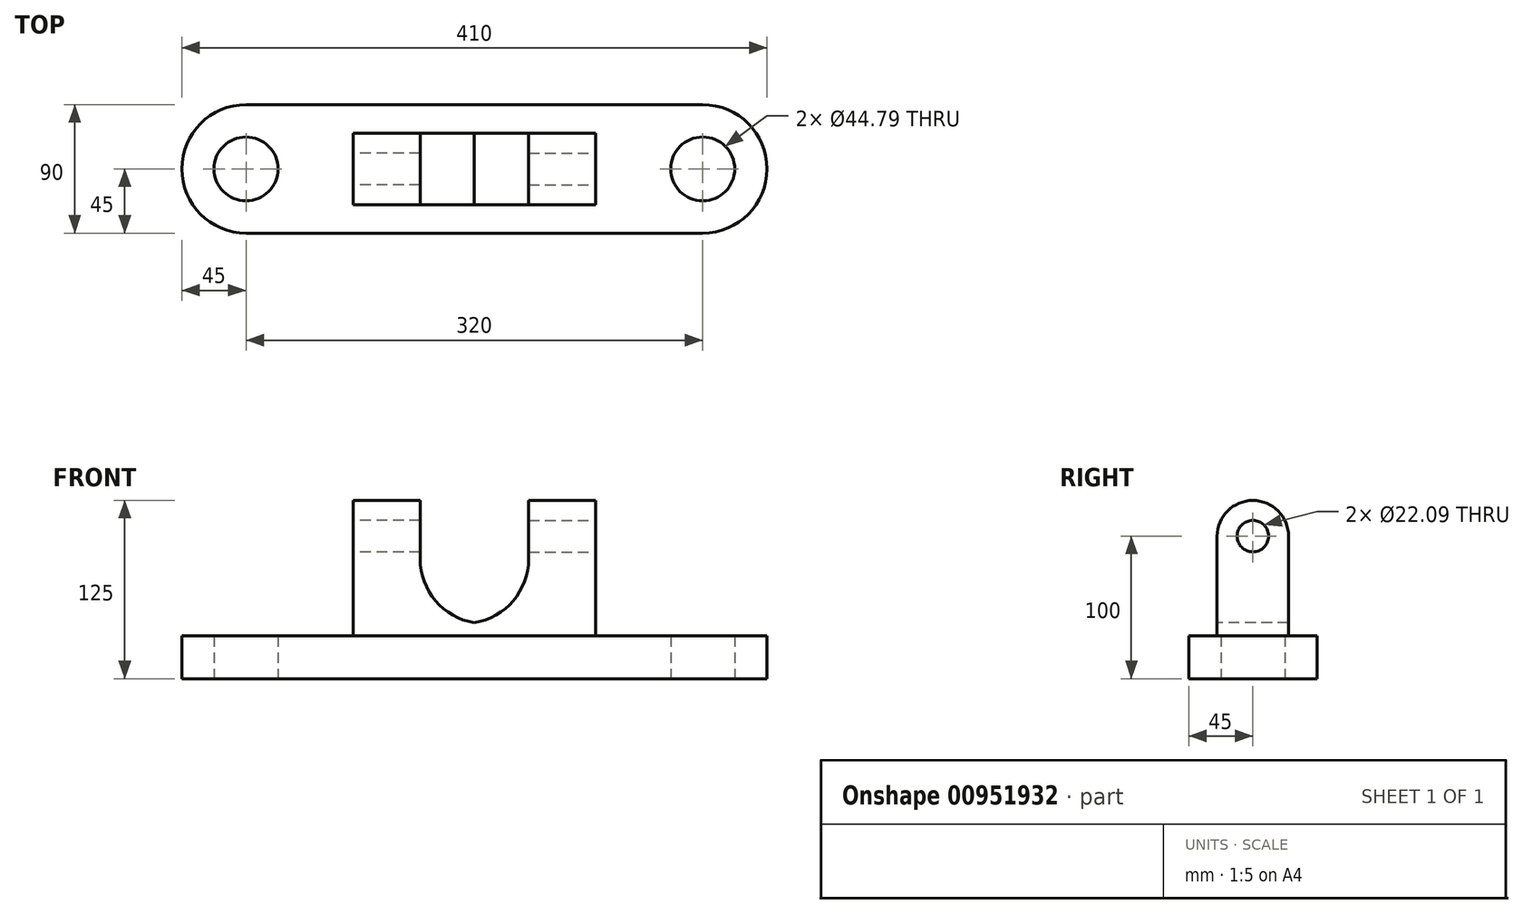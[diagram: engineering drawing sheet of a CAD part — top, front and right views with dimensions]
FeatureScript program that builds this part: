
annotation { "Feature Type Name" : "Feature", "Feature Type Description" : "" }
export const myFeature = defineFeature(function(context is Context, id is Id, definition is map)
    precondition{}
    {
        {
            var Q0;
            Q0=qCreatedBy(makeId("Top.planeOp"),FACE);
            var sketch = newSketch(context, id + "F0", { "sketchPlane" : qUnion([Q0])});
            skLineSegment(sketch, "E0.bottom", {"start": v(0, 45) * mm, "end": v(-160, 45) * mm});
            skLineSegment(sketch, "E0.top", {"start": v(0, -45) * mm, "end": v(-160, -45) * mm});
            skLineSegment(sketch, "E0.left", {"start": v(0, 45) * mm, "end": v(0, -45) * mm});
            skLineSegment(sketch, "E1", {"start": v(0, 45) * mm, "end": v(0, 0) * mm});
            skLineSegment(sketch, "E2", {"start": v(0, -45) * mm, "end": v(0, 0) * mm});
            skArc(sketch, "E3", {"start": v(-160, 45) * mm, "mid": v(-205, 0) * mm, "end": v(-160, -45) * mm});
            skCircle(sketch, "E4", {"center": v(-160, 0) * mm, "radius": 22.4 * mm});
            skSolve(sketch);
        }
        {
            var Q0;
            Q0=makeQuery(id+"F0.imprint","IMPRINT",FACE,{"disambiguationData":[TD([[makeQuery(id+"F0.imprint","IMPRINT",EDGE,{"derivedFrom":sQuery(id+"F0.wireOp",EDGE,"E0.top")}),-1.0]])]});
            extrude(context, id + "F1", {"entities" : qUnion([Q0]), "depth" : 30 * mm, "offsetDistance" : 25 * mm});
        }
        {
            var Q0;
            Q0=makeQuery(id+"F1.opExtrude","CAP_FACE",FACE,{"disambiguationData":[OSD([sQuery(id+"F0.wireOp",EDGE,"E0.top"),sQuery(id+"F0.wireOp",EDGE,"E1"),sQuery(id+"F0.wireOp",EDGE,"E2"),sQuery(id+"F0.wireOp",EDGE,"E0.bottom"),sQuery(id+"F0.wireOp",EDGE,"E3"),sQuery(id+"F0.wireOp",EDGE,"E4")])],"isStart":false});
            var sketch = newSketch(context, id + "F2", { "sketchPlane" : qUnion([Q0])});
            skLineSegment(sketch, "E5", {"start": v(0, 45) * mm, "end": v(0, 25) * mm});
            skLineSegment(sketch, "E6", {"start": v(0, 25) * mm, "end": v(0, -25) * mm});
            skLineSegment(sketch, "E7", {"start": v(0, -25) * mm, "end": v(0, -45) * mm});
            skLineSegment(sketch, "E8", {"start": v(0, -45) * mm, "end": v(0, -25) * mm});
            skLineSegment(sketch, "E9.bottom", {"start": v(0, 25) * mm, "end": v(0, 25) * mm});
            skLineSegment(sketch, "E9.top", {"start": v(0, -25) * mm, "end": v(0, -25) * mm});
            skLineSegment(sketch, "E10.bottom", {"start": v(0, 25) * mm, "end": v(-85, 25) * mm});
            skLineSegment(sketch, "E10.top", {"start": v(0, -25) * mm, "end": v(-85, -25) * mm});
            skLineSegment(sketch, "E10.right", {"start": v(-85, 25) * mm, "end": v(-85, -25) * mm});
            skSolve(sketch);
        }
        {
            var Q0;
            Q0=makeQuery(id+"F2.imprint","IMPRINT",FACE,{"disambiguationData":[TD([[makeQuery(id+"F2.imprint","IMPRINT",EDGE,{"derivedFrom":sQuery(id+"F2.wireOp",EDGE,"E10.bottom")}),1.0]])]});
            extrude(context, id + "F3", {"entities" : qUnion([Q0]), "operationType" : NewBodyOperationType.ADD, "depth" : 70 * mm, "offsetDistance" : 25 * mm});
        }
        {
            var Q0;
            Q0=makeQuery(id+"F3.opExtrude","SWEPT_FACE",FACE,{"disambiguationData":[OSD([sQuery(id+"F2.wireOp",EDGE,"E10.top")])]});
            var sketch = newSketch(context, id + "F4", { "sketchPlane" : qUnion([Q0])});
            skLineSegment(sketch, "E11.bottom", {"start": v(0, 100) * mm, "end": v(-38, 100) * mm});
            skLineSegment(sketch, "E11.top", {"start": v(0, 39.26) * mm, "end": v(-38, 39.26) * mm});
            skLineSegment(sketch, "E11.left", {"start": v(0, 100) * mm, "end": v(0, 39.26) * mm});
            skLineSegment(sketch, "E11.right", {"start": v(-38, 100) * mm, "end": v(-38, 39.26) * mm});
            skLineSegment(sketch, "E12", {"start": v(-85, 100) * mm, "end": v(-38, 100) * mm});
            skSolve(sketch);
        }
        {
            var Q0;
            Q0=makeQuery(id+"F4.imprint","IMPRINT",FACE,{"disambiguationData":[TD([[makeQuery(id+"F4.imprint","IMPRINT",EDGE,{"derivedFrom":sQuery(id+"F4.wireOp",EDGE,"E11.bottom")}),1.0]])]});
            extrude(context, id + "F5", {"entities" : qUnion([Q0]), "operationType" : NewBodyOperationType.REMOVE, "oppositeDirection" : true, "depth" : 50 * mm, "offsetDistance" : 25 * mm});
        }
        {
            var Q0;
            Q0=makeQuery(id+"F5.boolean.opBoolean","COPY",EDGE,{"derivedFrom":makeQuery(id+"F5.opExtrude","SWEPT_EDGE",EDGE,{"disambiguationData":[OSD([sQuery(id+"F4.wireOp",EDGE,"E11.top"),sQuery(id+"F4.wireOp",EDGE,"E11.right")])]})});
            fillet(context, id + "F6", {"entities" : qUnion([Q0]), "radius" : 45.4 * mm, "tangentPropagation" : true, "allowEdgeOverflow" : false});
        }
        {
            var Q0;
            Q0=makeQuery(id+"F3.opExtrude","SWEPT_FACE",FACE,{"disambiguationData":[OSD([sQuery(id+"F2.wireOp",EDGE,"E10.right")])]});
            var sketch = newSketch(context, id + "F7", { "sketchPlane" : qUnion([Q0])});
            skArc(sketch, "E13", {"start": v(25, 100) * mm, "mid": v(0, 125) * mm, "end": v(-25, 100) * mm});
            skSolve(sketch);
        }
        {
            var Q0;
            Q0=makeQuery(id+"F7.imprint","IMPRINT",FACE,{"disambiguationData":[TD([[makeQuery(id+"F7.imprint","IMPRINT",EDGE,{"derivedFrom":sQuery(id+"F7.wireOp",EDGE,"E13")}),1.0]])]});
            extrude(context, id + "F8", {"entities" : qUnion([Q0]), "operationType" : NewBodyOperationType.ADD, "oppositeDirection" : true, "depth" : 47 * mm, "offsetDistance" : 25 * mm});
        }
        {
            var Q0;
            {var subQ0=sQuery(id+"F2.wireOp",EDGE,"E10.right");Q0=makeQuery(id+"F8.boolean.opBoolean","MERGE",FACE,{"derivedFrom":[makeQuery(id+"F3.opExtrude","SWEPT_FACE",FACE,{"disambiguationData":[OSD([subQ0])]}),makeQuery(id+"F8.opExtrude","CAP_FACE",FACE,{"disambiguationData":[OSD([subQ0,sQuery(id+"F7.wireOp",EDGE,"E13")])],"isStart":true})]});}
            var sketch = newSketch(context, id + "F9", { "sketchPlane" : qUnion([Q0])});
            skCircle(sketch, "E14", {"center": v(0, 100) * mm, "radius": 11.04 * mm});
            skSolve(sketch);
        }
        {
            var Q0;
            Q0=makeQuery(id+"F9.imprint","IMPRINT",FACE,{"disambiguationData":[TD([[makeQuery(id+"F9.imprint","IMPRINT",EDGE,{"derivedFrom":sQuery(id+"F9.wireOp",EDGE,"E14")}),1.0]])]});
            extrude(context, id + "F10", {"entities" : qUnion([Q0]), "operationType" : NewBodyOperationType.REMOVE, "oppositeDirection" : true, "depth" : 47 * mm, "offsetDistance" : 25 * mm});
        }
        {
            var Q0;
            Q0=makeQuery(id+"F1.opExtrude","SWEPT_BODY",BODY,{"disambiguationData":[OSD([sQuery(id+"F0.wireOp",EDGE,"E0.top"),sQuery(id+"F0.wireOp",EDGE,"E1"),sQuery(id+"F0.wireOp",EDGE,"E2"),sQuery(id+"F0.wireOp",EDGE,"E0.bottom"),sQuery(id+"F0.wireOp",EDGE,"E3"),sQuery(id+"F0.wireOp",EDGE,"E4")])]});
            var Q1;
            Q1=makeQuery(id+"F3.boolean.opBoolean","MERGE",FACE,{"derivedFrom":[makeQuery(id+"F1.opExtrude","SWEPT_FACE",FACE,{"disambiguationData":[OSD([sQuery(id+"F0.wireOp",EDGE,"E1"),sQuery(id+"F0.wireOp",EDGE,"E2")])]}),makeQuery(id+"F3.opExtrude","SWEPT_FACE",FACE,{"disambiguationData":[OSD([sQuery(id+"F2.wireOp",EDGE,"E6")])]})]});
            mirror(context, id + "F11", {"operationType" : NewBodyOperationType.ADD, "entities" : qUnion([Q0]), "mirrorPlane" : qUnion([Q1])});
        }
    });
